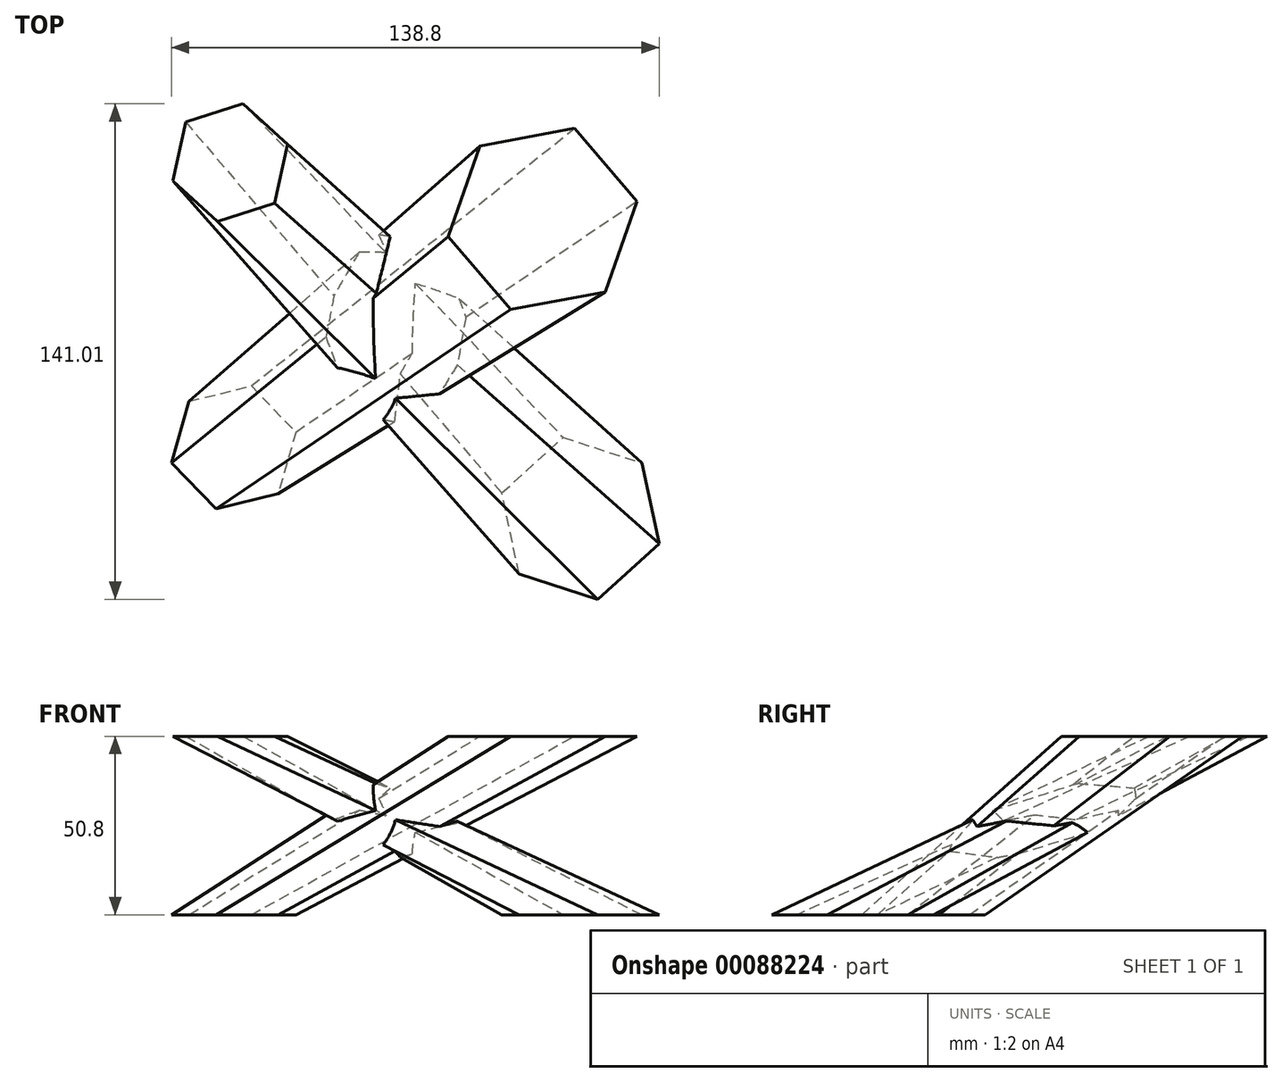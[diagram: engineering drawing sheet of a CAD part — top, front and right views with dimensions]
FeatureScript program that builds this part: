
annotation { "Feature Type Name" : "Feature", "Feature Type Description" : "" }
export const myFeature = defineFeature(function(context is Context, id is Id, definition is map)
    precondition{}
    {
        {
            var Q0;
            Q0=qCreatedBy(makeId("Top.planeOp"),FACE);
            cPlane(context, id + "F0", {"entities" : qUnion([Q0]), "cplaneType" : CPlaneType.OFFSET, "offset" : 50.8 * mm, "width" : 152.4 * mm, "height" : 152.4 * mm});
        }
        {
            var Q0;
            Q0=qCreatedBy(id+"F0.planeOp",FACE);
            var sketch = newSketch(context, id + "F1", { "sketchPlane" : qUnion([Q0])});
            skCircle(sketch, "E0.cCircle", {"center": v(36.04, 33.98) * mm, "radius": 23.66 * mm, "construction": true});
            skLineSegment(sketch, "E0.0", {"start": v(9.19, 28.93) * mm, "end": v(18.23, 54.7) * mm});
            skLineSegment(sketch, "E0.1", {"start": v(18.23, 54.7) * mm, "end": v(45.09, 59.76) * mm});
            skLineSegment(sketch, "E0.2", {"start": v(45.09, 59.76) * mm, "end": v(62.9, 39.04) * mm});
            skLineSegment(sketch, "E0.3", {"start": v(62.9, 39.04) * mm, "end": v(53.84, 13.26) * mm});
            skLineSegment(sketch, "E0.4", {"start": v(53.84, 13.26) * mm, "end": v(27, 8.2) * mm});
            skLineSegment(sketch, "E0.5", {"start": v(27, 8.2) * mm, "end": v(9.19, 28.93) * mm});
            skPoint(sketch, "E0.0.midPoint", {"position": v(13.71, 41.82) * mm});
            skSolve(sketch);
        }
        {
            var Q0;
            Q0=qCreatedBy(makeId("Top.planeOp"),FACE);
            var sketch = newSketch(context, id + "F2", { "sketchPlane" : qUnion([Q0])});
            skCircle(sketch, "E1.cCircle", {"center": v(-51.9, -31.04) * mm, "radius": 15.8 * mm, "construction": true});
            skLineSegment(sketch, "E1.0", {"start": v(-46.88, -13.52) * mm, "end": v(-34.21, -26.63) * mm});
            skLineSegment(sketch, "E1.1", {"start": v(-34.21, -26.63) * mm, "end": v(-39.24, -44.16) * mm});
            skLineSegment(sketch, "E1.2", {"start": v(-39.24, -44.16) * mm, "end": v(-56.93, -48.57) * mm});
            skLineSegment(sketch, "E1.3", {"start": v(-56.93, -48.57) * mm, "end": v(-69.6, -35.45) * mm});
            skLineSegment(sketch, "E1.4", {"start": v(-69.6, -35.45) * mm, "end": v(-64.57, -17.93) * mm});
            skLineSegment(sketch, "E1.5", {"start": v(-64.57, -17.93) * mm, "end": v(-46.88, -13.52) * mm});
            skPoint(sketch, "E1.0.midPoint", {"position": v(-40.54, -20.08) * mm});
            skSolve(sketch);
        }
        {
            var Q0;
            Q0=makeQuery(id+"F2.imprint","IMPRINT",FACE,{"disambiguationData":[TD([[makeQuery(id+"F2.imprint","IMPRINT",EDGE,{"derivedFrom":sQuery(id+"F2.wireOp",EDGE,"E1.0")}),-1.0]])]});
            var Q1;
            Q1=makeQuery(id+"F1.imprint","IMPRINT",FACE,{"disambiguationData":[TD([[makeQuery(id+"F1.imprint","IMPRINT",EDGE,{"derivedFrom":sQuery(id+"F1.wireOp",EDGE,"E0.0")}),-1.0]])]});
            loft(context, id + "F3", {"sheetProfilesArray" : [{ "sheetProfileEntities" : qUnion([Q0]) }, { "sheetProfileEntities" : qUnion([Q1]) }]});
        }
        {
            var Q0;
            Q0=qCreatedBy(makeId("Top.planeOp"),FACE);
            var sketch = newSketch(context, id + "F4", { "sketchPlane" : qUnion([Q0])});
            skCircle(sketch, "E2.cCircle", {"center": v(46.81, -51.22) * mm, "radius": 20.38 * mm, "construction": true});
            skLineSegment(sketch, "E2.0", {"start": v(41.88, -28.2) * mm, "end": v(64.27, -35.45) * mm});
            skLineSegment(sketch, "E2.1", {"start": v(64.27, -35.45) * mm, "end": v(69.2, -58.46) * mm});
            skLineSegment(sketch, "E2.2", {"start": v(69.2, -58.46) * mm, "end": v(51.74, -74.23) * mm});
            skLineSegment(sketch, "E2.3", {"start": v(51.74, -74.23) * mm, "end": v(29.35, -66.99) * mm});
            skLineSegment(sketch, "E2.4", {"start": v(29.35, -66.99) * mm, "end": v(24.42, -43.98) * mm});
            skLineSegment(sketch, "E2.5", {"start": v(24.42, -43.98) * mm, "end": v(41.88, -28.2) * mm});
            skPoint(sketch, "E2.0.midPoint", {"position": v(53.08, -31.83) * mm});
            skSolve(sketch);
        }
        {
            var Q0;
            Q0=qCreatedBy(id+"F0.planeOp",FACE);
            var sketch = newSketch(context, id + "F5", { "sketchPlane" : qUnion([Q0])});
            skCircle(sketch, "E3.cCircle", {"center": v(-52.88, 50.04) * mm, "radius": 14.84 * mm, "construction": true});
            skLineSegment(sketch, "E3.0", {"start": v(-49.23, 66.78) * mm, "end": v(-36.56, 55.24) * mm});
            skLineSegment(sketch, "E3.1", {"start": v(-36.56, 55.24) * mm, "end": v(-40.22, 38.5) * mm});
            skLineSegment(sketch, "E3.2", {"start": v(-40.22, 38.5) * mm, "end": v(-56.54, 33.3) * mm});
            skLineSegment(sketch, "E3.3", {"start": v(-56.54, 33.3) * mm, "end": v(-69.2, 44.84) * mm});
            skLineSegment(sketch, "E3.4", {"start": v(-69.2, 44.84) * mm, "end": v(-65.55, 61.58) * mm});
            skLineSegment(sketch, "E3.5", {"start": v(-65.55, 61.58) * mm, "end": v(-49.23, 66.78) * mm});
            skPoint(sketch, "E3.0.midPoint", {"position": v(-42.9, 61.01) * mm});
            skSolve(sketch);
        }
        {
            var Q1;
            Q1=makeQuery(id+"F5.imprint","IMPRINT",FACE,{"disambiguationData":[TD([[makeQuery(id+"F5.imprint","IMPRINT",EDGE,{"derivedFrom":sQuery(id+"F5.wireOp",EDGE,"E3.0")}),-1.0]])]});
            var Q2;
            Q2=makeQuery(id+"F4.imprint","IMPRINT",FACE,{"disambiguationData":[TD([[makeQuery(id+"F4.imprint","IMPRINT",EDGE,{"derivedFrom":sQuery(id+"F4.wireOp",EDGE,"E2.0")}),-1.0]])]});
            loft(context, id + "F6", {"operationType" : NewBodyOperationType.ADD, "sheetProfilesArray" : [{ "sheetProfileEntities" : qUnion([Q1]) }, { "sheetProfileEntities" : qUnion([Q2]) }]});
        }
    });
